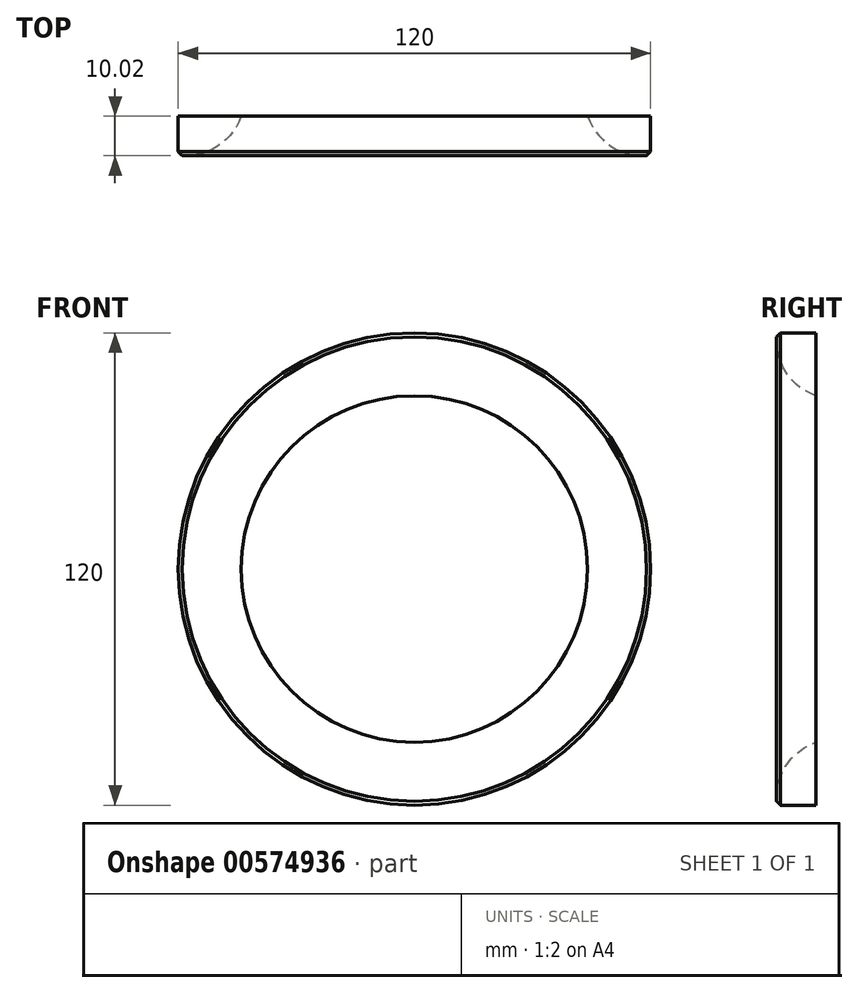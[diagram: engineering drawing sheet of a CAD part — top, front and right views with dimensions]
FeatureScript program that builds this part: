
annotation { "Feature Type Name" : "Feature", "Feature Type Description" : "" }
export const myFeature = defineFeature(function(context is Context, id is Id, definition is map)
    precondition{}
    {
        {
            var Q0;
            Q0=qCreatedBy(makeId("Right.planeOp"),FACE);
            var sketch = newSketch(context, id + "F0", { "sketchPlane" : qUnion([Q0])});
            skLineSegment(sketch, "E0", {"start": v(0, 0) * mm, "end": v(10, 0) * mm, "construction": true});
            skLineSegment(sketch, "E1", {"start": v(10, 0) * mm, "end": v(10, 44) * mm, "construction": true});
            skLineSegment(sketch, "E2", {"start": v(10, 44) * mm, "end": v(0, 59) * mm, "construction": true});
            skLineSegment(sketch, "E3", {"start": v(0, 59) * mm, "end": v(1, 60) * mm});
            skArc(sketch, "E4", {"start": v(0, 59) * mm, "mid": v(2.5, 49.83) * mm, "end": v(10, 44) * mm});
            skLineSegment(sketch, "E5", {"start": v(1, 60) * mm, "end": v(10, 60) * mm});
            skLineSegment(sketch, "E6", {"start": v(10, 60) * mm, "end": v(10, 44) * mm});
            skSolve(sketch);
        }
        {
            var Q0;
            Q0=makeQuery(id+"F0.imprint","IMPRINT",FACE,{"disambiguationData":[TD([[makeQuery(id+"F0.imprint","IMPRINT",EDGE,{"derivedFrom":sQuery(id+"F0.wireOp",EDGE,"E3")}),-1.0]])]});
            var Q1;
            Q1=sQuery(id+"F0.wireOp",EDGE,"E0");
            revolve(context, id + "F1", {"entities" : qUnion([Q0]), "axis" : qUnion([Q1]), "revolveType" : RevolveType.FULL});
        }
    });
